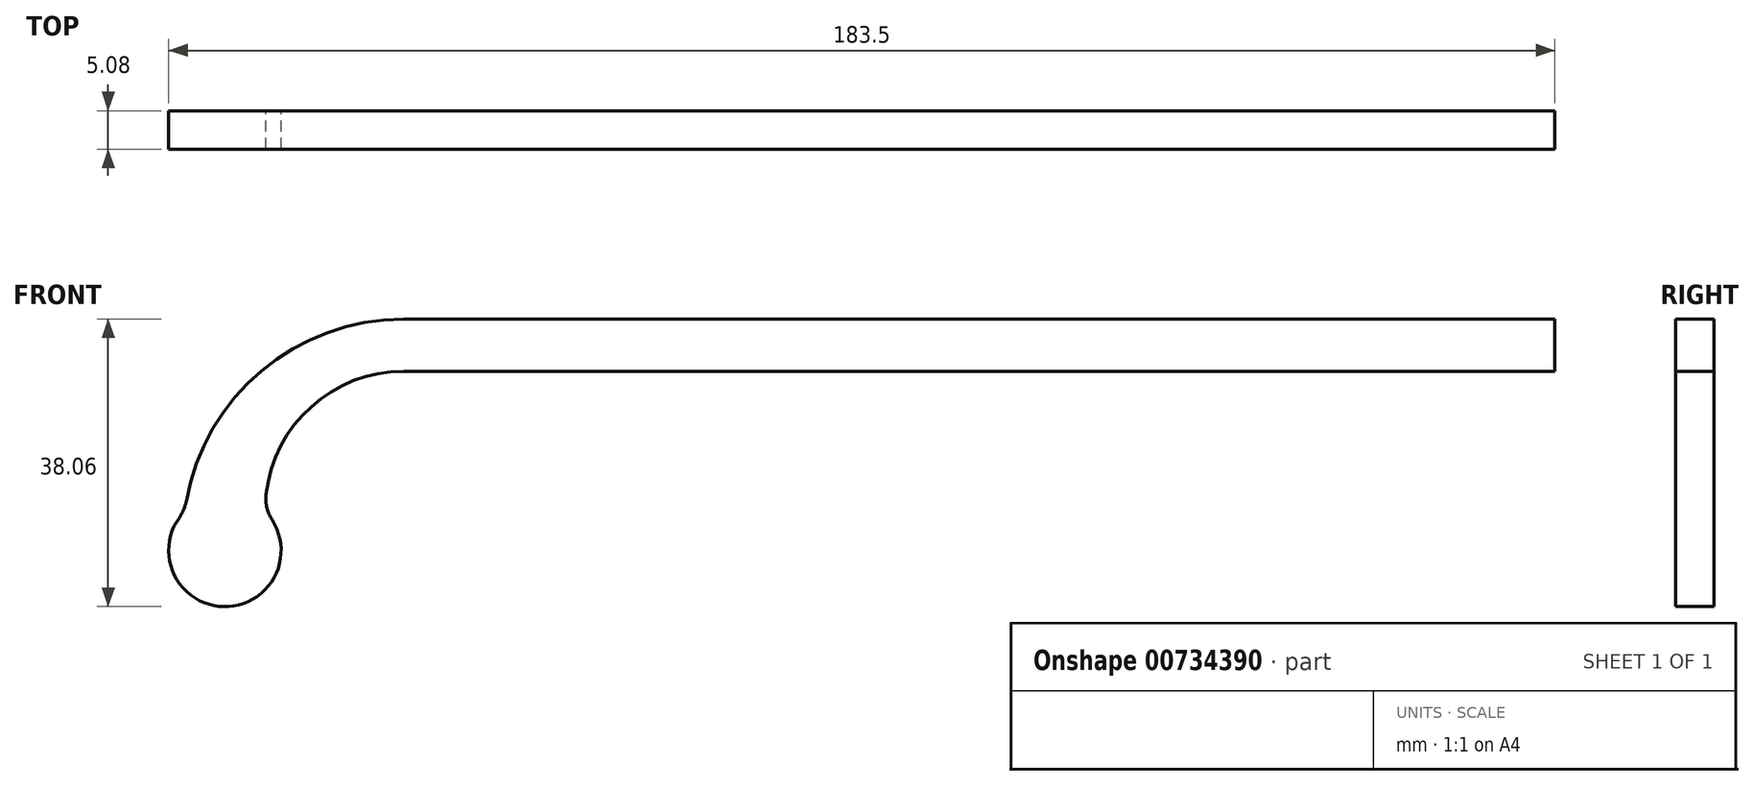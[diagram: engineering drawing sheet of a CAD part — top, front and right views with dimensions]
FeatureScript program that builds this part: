
annotation { "Feature Type Name" : "Feature", "Feature Type Description" : "" }
export const myFeature = defineFeature(function(context is Context, id is Id, definition is map)
    precondition{}
    {
        {
            var Q0;
            Q0=qCreatedBy(makeId("Front.planeOp"),FACE);
            var sketch = newSketch(context, id + "F0", { "sketchPlane" : qUnion([Q0])});
            skLineSegment(sketch, "E0", {"start": v(-75.05, 35.12) * mm, "end": v(77.35, 35.12) * mm});
            skLineSegment(sketch, "E1", {"start": v(77.35, 35.12) * mm, "end": v(77.35, 28.2) * mm});
            skLineSegment(sketch, "E2", {"start": v(77.35, 28.2) * mm, "end": v(-75.05, 28.2) * mm});
            skArc(sketch, "E3", {"start": v(-75.05, 28.2) * mm, "mid": v(-88.08, 22.77) * mm, "end": v(-93.37, 9.68) * mm});
            skArc(sketch, "E4", {"start": v(-75.05, 35.12) * mm, "mid": v(-94.33, 27.86) * mm, "end": v(-104.05, 9.68) * mm});
            skArc(sketch, "E5", {"start": v(-104.05, 9.68) * mm, "mid": v(-98.71, -2.94) * mm, "end": v(-93.37, 9.68) * mm});
            skSolve(sketch);
        }
        {
            var Q0;
            Q0 = qSketchRegion(id + "F0", true);
            extrude(context, id + "F1", {"entities" : qUnion([Q0]), "depth" : 5.08 * mm, "offsetDistance" : 25.4 * mm});
        }
        {
            var Q0;
            Q0=makeQuery(id+"F1.opExtrude","SWEPT_EDGE",EDGE,{"disambiguationData":[OSD([sQuery(id+"F0.wireOp",EDGE,"E4"),sQuery(id+"F0.wireOp",EDGE,"E5")])]});
            var Q1;
            Q1=makeQuery(id+"F1.opExtrude","SWEPT_EDGE",EDGE,{"disambiguationData":[OSD([sQuery(id+"F0.wireOp",EDGE,"E3"),sQuery(id+"F0.wireOp",EDGE,"E5")])]});
            var Q2;
            Q2=makeQuery(id+"F1.opExtrude","SWEPT_EDGE",EDGE,{"disambiguationData":[OSD([sQuery(id+"F0.wireOp",EDGE,"E0"),sQuery(id+"F0.wireOp",EDGE,"E4")])]});
            var Q3;
            Q3=makeQuery(id+"F1.opExtrude","SWEPT_EDGE",EDGE,{"disambiguationData":[OSD([sQuery(id+"F0.wireOp",EDGE,"E2"),sQuery(id+"F0.wireOp",EDGE,"E3")])]});
            fillet(context, id + "F2", {"entities" : qUnion([Q0, Q1, Q2, Q3]), "radius" : 5.08 * mm, "tangentPropagation" : true, "allowEdgeOverflow" : false});
        }
    });
